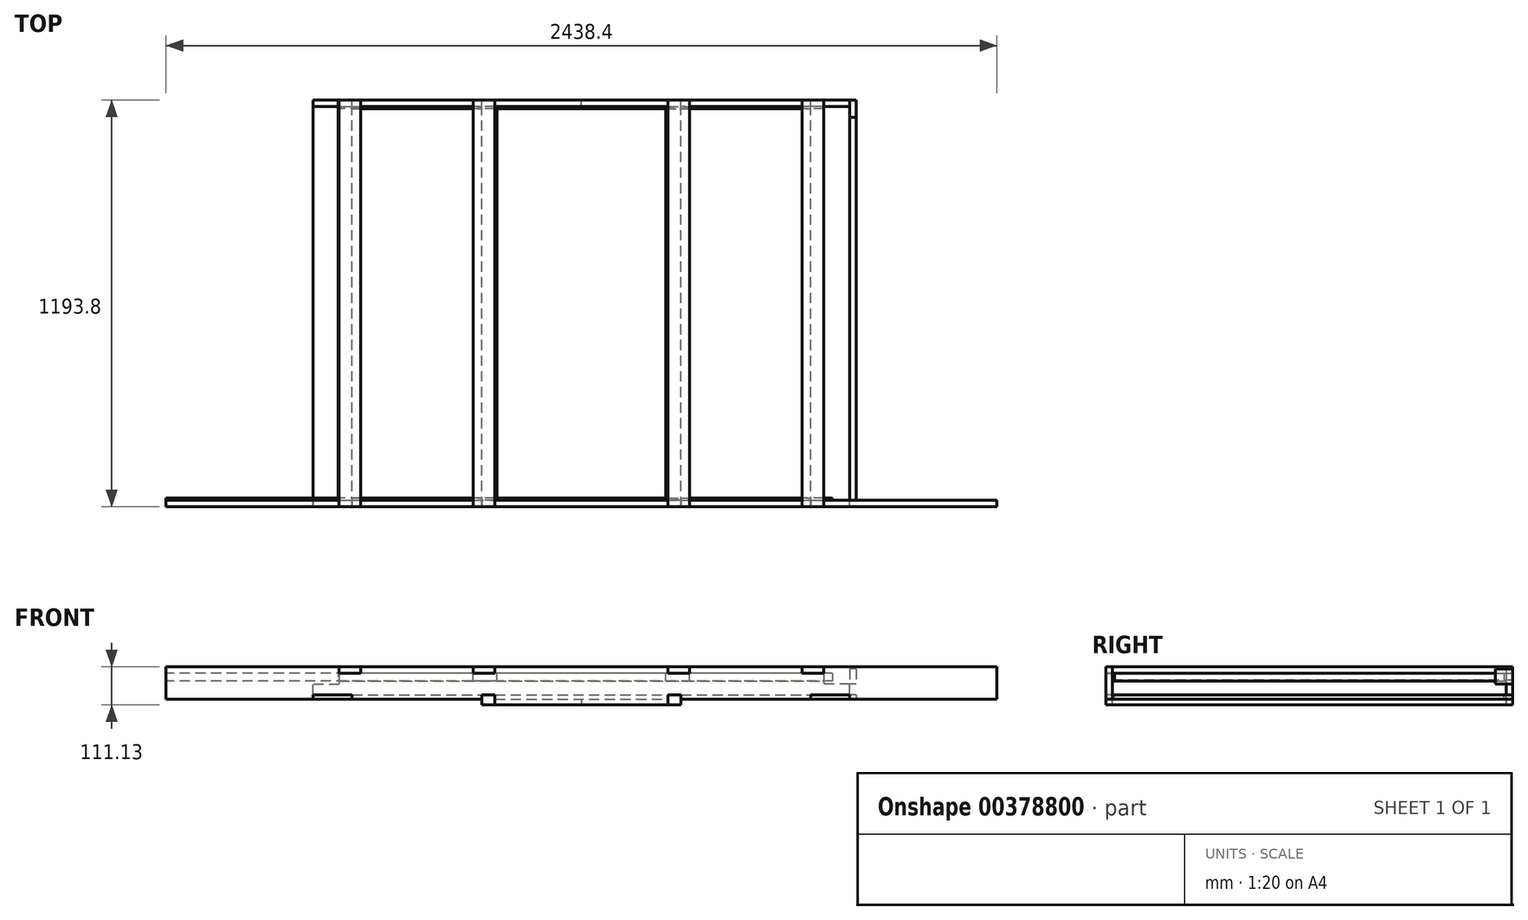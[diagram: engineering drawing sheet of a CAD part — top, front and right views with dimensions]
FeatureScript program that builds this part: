
annotation { "Feature Type Name" : "Feature", "Feature Type Description" : "" }
export const myFeature = defineFeature(function(context is Context, id is Id, definition is map)
    precondition{}
    {
        {
            var Q0;
            Q0=qCreatedBy(makeId("Front.planeOp"),FACE);
            var sketch = newSketch(context, id + "F0", { "sketchPlane" : qUnion([Q0])});
            skLineSegment(sketch, "E0.bottom", {"start": v(0, 0) * mm, "end": v(787.4, 0) * mm});
            skLineSegment(sketch, "E0.top", {"start": v(0, 95.25) * mm, "end": v(787.4, 95.25) * mm});
            skLineSegment(sketch, "E0.left", {"start": v(0, 0) * mm, "end": v(0, 95.25) * mm});
            skLineSegment(sketch, "E0.right", {"start": v(787.4, 0) * mm, "end": v(787.4, 95.25) * mm});
            skLineSegment(sketch, "E1.bottom", {"start": v(0, 95.25) * mm, "end": v(76.2, 95.25) * mm});
            skLineSegment(sketch, "E1.top", {"start": v(0, 44.45) * mm, "end": v(76.2, 44.45) * mm});
            skLineSegment(sketch, "E1.left", {"start": v(0, 95.25) * mm, "end": v(0, 44.45) * mm});
            skLineSegment(sketch, "E1.right", {"start": v(76.2, 95.25) * mm, "end": v(76.2, 44.45) * mm});
            skLineSegment(sketch, "E2.bottom", {"start": v(76.2, 95.25) * mm, "end": v(139.7, 95.25) * mm});
            skLineSegment(sketch, "E2.top", {"start": v(76.2, 76.2) * mm, "end": v(139.7, 76.2) * mm});
            skLineSegment(sketch, "E2.left", {"start": v(76.2, 95.25) * mm, "end": v(76.2, 76.2) * mm});
            skLineSegment(sketch, "E2.right", {"start": v(139.7, 95.25) * mm, "end": v(139.7, 76.2) * mm});
            skLineSegment(sketch, "E3.bottom", {"start": v(0, 0) * mm, "end": v(114.3, 0) * mm});
            skLineSegment(sketch, "E3.top", {"start": v(0, 12.7) * mm, "end": v(114.3, 12.7) * mm});
            skLineSegment(sketch, "E3.left", {"start": v(0, 0) * mm, "end": v(0, 12.7) * mm});
            skLineSegment(sketch, "E3.right", {"start": v(114.3, 0) * mm, "end": v(114.3, 12.7) * mm});
            skLineSegment(sketch, "E4.MirrorCS", {"start": v(1574.8, 0) * mm, "end": v(1574.8, 12.7) * mm});
            skLineSegment(sketch, "E5.MirrorCS", {"start": v(1498.6, 95.25) * mm, "end": v(1498.6, 76.2) * mm});
            skLineSegment(sketch, "E6.MirrorCS", {"start": v(1574.8, 0) * mm, "end": v(1574.8, 95.25) * mm});
            skLineSegment(sketch, "E7.MirrorCS", {"start": v(1498.6, 95.25) * mm, "end": v(1498.6, 44.45) * mm});
            skLineSegment(sketch, "E8.MirrorCS", {"start": v(1460.5, 0) * mm, "end": v(1460.5, 12.7) * mm});
            skLineSegment(sketch, "E9.MirrorCS", {"start": v(1435.1, 95.25) * mm, "end": v(1435.1, 76.2) * mm});
            skLineSegment(sketch, "E10.MirrorCS", {"start": v(1574.8, 44.45) * mm, "end": v(1498.6, 44.45) * mm});
            skLineSegment(sketch, "E11.MirrorCS", {"start": v(1574.8, 95.25) * mm, "end": v(1574.8, 44.45) * mm});
            skLineSegment(sketch, "E12.MirrorCS", {"start": v(1574.8, 95.25) * mm, "end": v(787.4, 95.25) * mm});
            skLineSegment(sketch, "E13.MirrorCS", {"start": v(1574.8, 0) * mm, "end": v(787.4, 0) * mm});
            skLineSegment(sketch, "E14.MirrorCS", {"start": v(1498.6, 76.2) * mm, "end": v(1435.1, 76.2) * mm});
            skLineSegment(sketch, "E15.MirrorCS", {"start": v(1574.8, 95.25) * mm, "end": v(1498.6, 95.25) * mm});
            skLineSegment(sketch, "E16.MirrorCS", {"start": v(1574.8, 0) * mm, "end": v(1460.5, 0) * mm});
            skLineSegment(sketch, "E17.MirrorCS", {"start": v(1498.6, 95.25) * mm, "end": v(1435.1, 95.25) * mm});
            skLineSegment(sketch, "E18.MirrorCS", {"start": v(1574.8, 12.7) * mm, "end": v(1460.5, 12.7) * mm});
            skLineSegment(sketch, "E19.bottom", {"start": v(533.4, 95.25) * mm, "end": v(469.9, 95.25) * mm});
            skLineSegment(sketch, "E19.top", {"start": v(533.4, 76.2) * mm, "end": v(469.9, 76.2) * mm});
            skLineSegment(sketch, "E19.left", {"start": v(533.4, 95.25) * mm, "end": v(533.4, 76.2) * mm});
            skLineSegment(sketch, "E19.right", {"start": v(469.9, 95.25) * mm, "end": v(469.9, 76.2) * mm});
            skLineSegment(sketch, "E20.MirrorCS", {"start": v(1041.4, 95.25) * mm, "end": v(1041.4, 76.2) * mm});
            skLineSegment(sketch, "E21.MirrorCS", {"start": v(1104.9, 95.25) * mm, "end": v(1104.9, 76.2) * mm});
            skLineSegment(sketch, "E22.MirrorCS", {"start": v(1041.4, 95.25) * mm, "end": v(1104.9, 95.25) * mm});
            skLineSegment(sketch, "E23.MirrorCS", {"start": v(1041.4, 76.2) * mm, "end": v(1104.9, 76.2) * mm});
            skLineSegment(sketch, "E24.bottom", {"start": v(533.4, 0) * mm, "end": v(495.3, 0) * mm});
            skLineSegment(sketch, "E24.top", {"start": v(533.4, 12.7) * mm, "end": v(495.3, 12.7) * mm});
            skLineSegment(sketch, "E24.left", {"start": v(533.4, 0) * mm, "end": v(533.4, 12.7) * mm});
            skLineSegment(sketch, "E24.right", {"start": v(495.3, 0) * mm, "end": v(495.3, 12.7) * mm});
            skLineSegment(sketch, "E25.bottom", {"start": v(787.4, 0) * mm, "end": v(533.4, 0) * mm});
            skLineSegment(sketch, "E25.top", {"start": v(787.4, -15.87) * mm, "end": v(533.4, -15.87) * mm});
            skLineSegment(sketch, "E25.left", {"start": v(787.4, 0) * mm, "end": v(787.4, -15.87) * mm});
            skLineSegment(sketch, "E25.right", {"start": v(533.4, 0) * mm, "end": v(533.4, -15.87) * mm});
            skLineSegment(sketch, "E26.MirrorCS", {"start": v(1079.5, 0) * mm, "end": v(1079.5, 12.7) * mm});
            skLineSegment(sketch, "E27.MirrorCS", {"start": v(1041.4, 0) * mm, "end": v(1041.4, 12.7) * mm});
            skLineSegment(sketch, "E28.MirrorCS", {"start": v(1041.4, 0) * mm, "end": v(1041.4, -15.87) * mm});
            skLineSegment(sketch, "E29.MirrorCS", {"start": v(1041.4, 0) * mm, "end": v(1079.5, 0) * mm});
            skLineSegment(sketch, "E30.MirrorCS", {"start": v(787.4, -15.87) * mm, "end": v(1041.4, -15.87) * mm});
            skLineSegment(sketch, "E31.MirrorCS", {"start": v(787.4, 0) * mm, "end": v(1041.4, 0) * mm});
            skLineSegment(sketch, "E32.MirrorCS", {"start": v(1041.4, 12.7) * mm, "end": v(1079.5, 12.7) * mm});
            skSolve(sketch);
        }
        {
            var Q0;
            Q0=makeQuery(id+"F0.imprint","IMPRINT",FACE,{"disambiguationData":[TD([[makeQuery(id+"F0.imprint","IMPRINT",EDGE,{"derivedFrom":sQuery(id+"F0.wireOp",EDGE,"E0.bottom")}),1.0]])]});
            var Q1;
            {var subQ1=sQuery(id+"F0.wireOp",EDGE,"E0.right");Q1=makeQuery(id+"F0.imprint","IMPRINT",FACE,{"disambiguationData":[TD([[makeQuery(id+"F0.imprint","IMPRINT",EDGE,{"derivedFrom":subQ1}),-1.0]])]});}
            var Q2;
            Q2=makeQuery(id+"F0.imprint","IMPRINT",FACE,{"disambiguationData":[TD([[makeQuery(id+"F0.imprint","IMPRINT",EDGE,{"derivedFrom":sQuery(id+"F0.wireOp",EDGE,"E25.bottom")}),1.0]])]});
            var Q3;
            Q3=makeQuery(id+"F0.imprint","IMPRINT",FACE,{"disambiguationData":[TD([[makeQuery(id+"F0.imprint","IMPRINT",EDGE,{"derivedFrom":sQuery(id+"F0.wireOp",EDGE,"E25.left")}),1.0]])]});
            extrude(context, id + "F1", {"entities" : qUnion([Q0, Q1, Q2, Q3]), "depth" : 19.05 * mm});
        }
        {
            var Q0;
            Q0=makeQuery(id+"F1.opExtrude","CAP_FACE",FACE,{"disambiguationData":[OSD([sQuery(id+"F0.wireOp",EDGE,"E0.bottom"),sQuery(id+"F0.wireOp",EDGE,"E0.top"),sQuery(id+"F0.wireOp",EDGE,"E0.left"),sQuery(id+"F0.wireOp",EDGE,"E1.top"),sQuery(id+"F0.wireOp",EDGE,"E1.right"),sQuery(id+"F0.wireOp",EDGE,"E2.top"),sQuery(id+"F0.wireOp",EDGE,"E2.right"),sQuery(id+"F0.wireOp",EDGE,"E3.top"),sQuery(id+"F0.wireOp",EDGE,"E3.right"),sQuery(id+"F0.wireOp",EDGE,"E6.MirrorCS"),sQuery(id+"F0.wireOp",EDGE,"E7.MirrorCS"),sQuery(id+"F0.wireOp",EDGE,"E8.MirrorCS"),sQuery(id+"F0.wireOp",EDGE,"E9.MirrorCS"),sQuery(id+"F0.wireOp",EDGE,"E10.MirrorCS"),sQuery(id+"F0.wireOp",EDGE,"E12.MirrorCS"),sQuery(id+"F0.wireOp",EDGE,"E13.MirrorCS"),sQuery(id+"F0.wireOp",EDGE,"E14.MirrorCS"),sQuery(id+"F0.wireOp",EDGE,"E18.MirrorCS"),sQuery(id+"F0.wireOp",EDGE,"E19.top"),sQuery(id+"F0.wireOp",EDGE,"E19.left"),sQuery(id+"F0.wireOp",EDGE,"E19.right"),sQuery(id+"F0.wireOp",EDGE,"E20.MirrorCS"),sQuery(id+"F0.wireOp",EDGE,"E21.MirrorCS"),sQuery(id+"F0.wireOp",EDGE,"E23.MirrorCS")])],"isStart":false});
            var sketch = newSketch(context, id + "F2", { "sketchPlane" : qUnion([Q0])});
            skLineSegment(sketch, "E33.bottom", {"start": v(114.3, 12.7) * mm, "end": v(1460.5, 12.7) * mm});
            skLineSegment(sketch, "E33.top", {"start": v(114.3, 0) * mm, "end": v(1460.5, 0) * mm});
            skLineSegment(sketch, "E33.left", {"start": v(114.3, 12.7) * mm, "end": v(114.3, 0) * mm});
            skLineSegment(sketch, "E33.right", {"start": v(1460.5, 12.7) * mm, "end": v(1460.5, 0) * mm});
            skSolve(sketch);
        }
        {
            var Q0;
            {var subQ0=sQuery(id+"F2.wireOp",EDGE,"E33.left");Q0=makeQuery(id+"F2.imprint","IMPRINT",FACE,{"disambiguationData":[TD([[makeQuery(id+"F2.imprint","IMPRINT",EDGE,{"derivedFrom":subQ0}),-1.0]])]});}
            var Q1;
            {var subQ0=sQuery(id+"F2.wireOp",EDGE,"E33.right");Q1=makeQuery(id+"F2.imprint","IMPRINT",FACE,{"disambiguationData":[TD([[makeQuery(id+"F2.imprint","IMPRINT",EDGE,{"derivedFrom":subQ0}),1.0]])]});}
            var Q2;
            {var subQ0=sQuery(id+"F2.wireOp",EDGE,"E33.bottom");var subQ1=makeQuery(id+"F1.opExtrude","CAP_EDGE",EDGE,{"disambiguationData":[OSD([sQuery(id+"F0.wireOp",EDGE,"E24.left"),sQuery(id+"F0.wireOp",EDGE,"E25.right")])],"isStart":false});var subQ2=makeQuery(id+"F2.imprint","INTERSECT",VERTEX,{"derivedFrom":[subQ1,subQ0]});var subQ3=makeQuery(id+"F1.opExtrude","CAP_EDGE",EDGE,{"disambiguationData":[OSD([sQuery(id+"F0.wireOp",EDGE,"E27.MirrorCS"),sQuery(id+"F0.wireOp",EDGE,"E28.MirrorCS")])],"isStart":false});var subQ4=makeQuery(id+"F2.imprint","INTERSECT",VERTEX,{"derivedFrom":[subQ3,subQ0]});Q2=makeQuery(id+"F2.imprint","IMPRINT",FACE,{"disambiguationData":[TD([[makeQuery(id+"F2.imprint","IMPRINT",EDGE,{"disambiguationData":[TD([[subQ2,-1.0],[subQ4,1.0]])],"derivedFrom":subQ0}),-1.0]])]});}
            extrude(context, id + "F3", {"entities" : qUnion([Q0, Q1, Q2]), "depth" : 6.35 * mm});
        }
        {
            var Q0;
            Q0=makeQuery(id+"F1.opExtrude","CAP_FACE",FACE,{"disambiguationData":[OSD([sQuery(id+"F0.wireOp",EDGE,"E0.bottom"),sQuery(id+"F0.wireOp",EDGE,"E0.top"),sQuery(id+"F0.wireOp",EDGE,"E0.left"),sQuery(id+"F0.wireOp",EDGE,"E1.top"),sQuery(id+"F0.wireOp",EDGE,"E1.right"),sQuery(id+"F0.wireOp",EDGE,"E2.top"),sQuery(id+"F0.wireOp",EDGE,"E2.right"),sQuery(id+"F0.wireOp",EDGE,"E3.top"),sQuery(id+"F0.wireOp",EDGE,"E3.right"),sQuery(id+"F0.wireOp",EDGE,"E6.MirrorCS"),sQuery(id+"F0.wireOp",EDGE,"E7.MirrorCS"),sQuery(id+"F0.wireOp",EDGE,"E8.MirrorCS"),sQuery(id+"F0.wireOp",EDGE,"E9.MirrorCS"),sQuery(id+"F0.wireOp",EDGE,"E10.MirrorCS"),sQuery(id+"F0.wireOp",EDGE,"E12.MirrorCS"),sQuery(id+"F0.wireOp",EDGE,"E13.MirrorCS"),sQuery(id+"F0.wireOp",EDGE,"E14.MirrorCS"),sQuery(id+"F0.wireOp",EDGE,"E18.MirrorCS"),sQuery(id+"F0.wireOp",EDGE,"E19.top"),sQuery(id+"F0.wireOp",EDGE,"E19.left"),sQuery(id+"F0.wireOp",EDGE,"E19.right"),sQuery(id+"F0.wireOp",EDGE,"E20.MirrorCS"),sQuery(id+"F0.wireOp",EDGE,"E21.MirrorCS"),sQuery(id+"F0.wireOp",EDGE,"E23.MirrorCS")])],"isStart":false});
            var sketch = newSketch(context, id + "F4", { "sketchPlane" : qUnion([Q0])});
            skLineSegment(sketch, "E34.bottom", {"start": v(76.2, 53.97) * mm, "end": v(1498.6, 53.97) * mm});
            skLineSegment(sketch, "E34.top", {"start": v(76.2, 76.2) * mm, "end": v(1498.6, 76.2) * mm});
            skLineSegment(sketch, "E34.left", {"start": v(76.2, 53.97) * mm, "end": v(76.2, 76.2) * mm});
            skLineSegment(sketch, "E34.right", {"start": v(1498.6, 53.97) * mm, "end": v(1498.6, 76.2) * mm});
            skSolve(sketch);
        }
        {
            var Q0;
            Q0=makeQuery(id+"F4.imprint","IMPRINT",FACE,{"disambiguationData":[TD([[makeQuery(id+"F4.imprint","IMPRINT",EDGE,{"derivedFrom":sQuery(id+"F4.wireOp",EDGE,"E34.bottom")}),1.0]])]});
            extrude(context, id + "F5", {"entities" : qUnion([Q0]), "depth" : 6.35 * mm});
        }
        {
            var Q0;
            Q0=qCreatedBy(makeId("Front.planeOp"),FACE);
            var sketch = newSketch(context, id + "F6", { "sketchPlane" : qUnion([Q0])});
            skLineSegment(sketch, "E35.bottom", {"start": v(139.7, 76.2) * mm, "end": v(76.2, 76.2) * mm});
            skLineSegment(sketch, "E35.top", {"start": v(139.7, 95.25) * mm, "end": v(76.2, 95.25) * mm});
            skLineSegment(sketch, "E35.left", {"start": v(139.7, 76.2) * mm, "end": v(139.7, 95.25) * mm});
            skLineSegment(sketch, "E35.right", {"start": v(76.2, 76.2) * mm, "end": v(76.2, 95.25) * mm});
            skLineSegment(sketch, "E36.bottom", {"start": v(469.9, 95.25) * mm, "end": v(533.4, 95.25) * mm});
            skLineSegment(sketch, "E36.top", {"start": v(469.9, 76.2) * mm, "end": v(533.4, 76.2) * mm});
            skLineSegment(sketch, "E36.left", {"start": v(469.9, 95.25) * mm, "end": v(469.9, 76.2) * mm});
            skLineSegment(sketch, "E36.right", {"start": v(533.4, 95.25) * mm, "end": v(533.4, 76.2) * mm});
            skLineSegment(sketch, "E37.bottom", {"start": v(1041.4, 76.2) * mm, "end": v(1104.9, 76.2) * mm});
            skLineSegment(sketch, "E37.top", {"start": v(1041.4, 95.25) * mm, "end": v(1104.9, 95.25) * mm});
            skLineSegment(sketch, "E37.left", {"start": v(1041.4, 76.2) * mm, "end": v(1041.4, 95.25) * mm});
            skLineSegment(sketch, "E37.right", {"start": v(1104.9, 76.2) * mm, "end": v(1104.9, 95.25) * mm});
            skLineSegment(sketch, "E38.bottom", {"start": v(1435.1, 76.2) * mm, "end": v(1498.6, 76.2) * mm});
            skLineSegment(sketch, "E38.top", {"start": v(1435.1, 95.25) * mm, "end": v(1498.6, 95.25) * mm});
            skLineSegment(sketch, "E38.left", {"start": v(1435.1, 76.2) * mm, "end": v(1435.1, 95.25) * mm});
            skLineSegment(sketch, "E38.right", {"start": v(1498.6, 76.2) * mm, "end": v(1498.6, 95.25) * mm});
            skLineSegment(sketch, "E39.bottom", {"start": v(1460.5, 0) * mm, "end": v(1574.8, 0) * mm});
            skLineSegment(sketch, "E39.top", {"start": v(1460.5, 12.7) * mm, "end": v(1574.8, 12.7) * mm});
            skLineSegment(sketch, "E39.left", {"start": v(1460.5, 0) * mm, "end": v(1460.5, 12.7) * mm});
            skLineSegment(sketch, "E39.right", {"start": v(1574.8, 0) * mm, "end": v(1574.8, 12.7) * mm});
            skLineSegment(sketch, "E40.bottom", {"start": v(114.3, 0) * mm, "end": v(0, 0) * mm});
            skLineSegment(sketch, "E40.top", {"start": v(114.3, 12.7) * mm, "end": v(0, 12.7) * mm});
            skLineSegment(sketch, "E40.left", {"start": v(114.3, 0) * mm, "end": v(114.3, 12.7) * mm});
            skLineSegment(sketch, "E40.right", {"start": v(0, 0) * mm, "end": v(0, 12.7) * mm});
            skLineSegment(sketch, "E41.bottom", {"start": v(533.4, -15.87) * mm, "end": v(495.3, -15.87) * mm});
            skLineSegment(sketch, "E41.top", {"start": v(533.4, 12.7) * mm, "end": v(495.3, 12.7) * mm});
            skLineSegment(sketch, "E41.left", {"start": v(533.4, -15.87) * mm, "end": v(533.4, 12.7) * mm});
            skLineSegment(sketch, "E41.right", {"start": v(495.3, -15.87) * mm, "end": v(495.3, 12.7) * mm});
            skLineSegment(sketch, "E42.bottom", {"start": v(1079.5, -15.87) * mm, "end": v(1041.4, -15.87) * mm});
            skLineSegment(sketch, "E42.top", {"start": v(1079.5, 12.7) * mm, "end": v(1041.4, 12.7) * mm});
            skLineSegment(sketch, "E42.left", {"start": v(1079.5, -15.87) * mm, "end": v(1079.5, 12.7) * mm});
            skLineSegment(sketch, "E42.right", {"start": v(1041.4, -15.87) * mm, "end": v(1041.4, 12.7) * mm});
            skSolve(sketch);
        }
        {
            var Q0;
            Q0=makeQuery(id+"F6.imprint","IMPRINT",FACE,{"disambiguationData":[TD([[makeQuery(id+"F6.imprint","IMPRINT",EDGE,{"derivedFrom":sQuery(id+"F6.wireOp",EDGE,"E35.bottom")}),-1.0]])]});
            var Q1;
            Q1=makeQuery(id+"F6.imprint","IMPRINT",FACE,{"disambiguationData":[TD([[makeQuery(id+"F6.imprint","IMPRINT",EDGE,{"derivedFrom":sQuery(id+"F6.wireOp",EDGE,"E36.bottom")}),-1.0]])]});
            var Q2;
            Q2=makeQuery(id+"F6.imprint","IMPRINT",FACE,{"disambiguationData":[TD([[makeQuery(id+"F6.imprint","IMPRINT",EDGE,{"derivedFrom":sQuery(id+"F6.wireOp",EDGE,"E38.bottom")}),1.0]])]});
            var Q3;
            Q3=makeQuery(id+"F6.imprint","IMPRINT",FACE,{"disambiguationData":[TD([[makeQuery(id+"F6.imprint","IMPRINT",EDGE,{"derivedFrom":sQuery(id+"F6.wireOp",EDGE,"E37.bottom")}),1.0]])]});
            var Q4;
            Q4=makeQuery(id+"F6.imprint","IMPRINT",FACE,{"disambiguationData":[TD([[makeQuery(id+"F6.imprint","IMPRINT",EDGE,{"derivedFrom":sQuery(id+"F6.wireOp",EDGE,"E39.bottom")}),1.0]])]});
            var Q5;
            Q5=makeQuery(id+"F6.imprint","IMPRINT",FACE,{"disambiguationData":[TD([[makeQuery(id+"F6.imprint","IMPRINT",EDGE,{"derivedFrom":sQuery(id+"F6.wireOp",EDGE,"E40.bottom")}),-1.0]])]});
            var Q6;
            Q6=makeQuery(id+"F6.imprint","IMPRINT",FACE,{"disambiguationData":[TD([[makeQuery(id+"F6.imprint","IMPRINT",EDGE,{"derivedFrom":sQuery(id+"F6.wireOp",EDGE,"E41.bottom")}),-1.0]])]});
            var Q7;
            Q7=makeQuery(id+"F6.imprint","IMPRINT",FACE,{"disambiguationData":[TD([[makeQuery(id+"F6.imprint","IMPRINT",EDGE,{"derivedFrom":sQuery(id+"F6.wireOp",EDGE,"E42.bottom")}),-1.0]])]});
            extrude(context, id + "F7", {"entities" : qUnion([Q0, Q1, Q2, Q3, Q4, Q5, Q6, Q7]), "depth" : 1193.8 * mm});
        }
        {
            var Q0;
            Q0=makeQuery(id+"F7.opExtrude","CAP_FACE",FACE,{"disambiguationData":[OSD([sQuery(id+"F6.wireOp",EDGE,"E38.bottom"),sQuery(id+"F6.wireOp",EDGE,"E38.top"),sQuery(id+"F6.wireOp",EDGE,"E38.left"),sQuery(id+"F6.wireOp",EDGE,"E38.right")])],"isStart":false});
            var sketch = newSketch(context, id + "F8", { "sketchPlane" : qUnion([Q0])});
            skLineSegment(sketch, "E43.bottom", {"start": v(292.1, 95.25) * mm, "end": v(-431.8, 95.25) * mm});
            skLineSegment(sketch, "E43.top", {"start": v(317.5, 0) * mm, "end": v(-431.8, 0) * mm});
            skLineSegment(sketch, "E43.right", {"start": v(-431.8, 95.25) * mm, "end": v(-431.8, 0) * mm});
            skLineSegment(sketch, "E44.bottom", {"start": v(76.2, 95.25) * mm, "end": v(139.7, 95.25) * mm});
            skLineSegment(sketch, "E44.top", {"start": v(76.2, 76.2) * mm, "end": v(139.7, 76.2) * mm});
            skLineSegment(sketch, "E44.left", {"start": v(76.2, 95.25) * mm, "end": v(76.2, 76.2) * mm});
            skLineSegment(sketch, "E44.right", {"start": v(139.7, 95.25) * mm, "end": v(139.7, 76.2) * mm});
            skLineSegment(sketch, "E45.bottom", {"start": v(469.9, 95.25) * mm, "end": v(533.4, 95.25) * mm});
            skLineSegment(sketch, "E45.top", {"start": v(469.9, 76.2) * mm, "end": v(533.4, 76.2) * mm});
            skLineSegment(sketch, "E45.left", {"start": v(469.9, 95.25) * mm, "end": v(469.9, 76.2) * mm});
            skLineSegment(sketch, "E45.right", {"start": v(533.4, 95.25) * mm, "end": v(533.4, 76.2) * mm});
            skLineSegment(sketch, "E46.MirrorCS", {"start": v(533.4, 76.2) * mm, "end": v(469.9, 76.2) * mm});
            skLineSegment(sketch, "E47.MirrorCS", {"start": v(139.7, 76.2) * mm, "end": v(76.2, 76.2) * mm});
            skLineSegment(sketch, "E48.MirrorCS", {"start": v(139.7, 95.25) * mm, "end": v(76.2, 95.25) * mm});
            skLineSegment(sketch, "E49.MirrorCS", {"start": v(533.4, 95.25) * mm, "end": v(469.9, 95.25) * mm});
            skLineSegment(sketch, "E50.bottom", {"start": v(1460.5, 0) * mm, "end": v(1574.8, 0) * mm});
            skLineSegment(sketch, "E50.top", {"start": v(1460.5, 12.7) * mm, "end": v(1574.8, 12.7) * mm});
            skLineSegment(sketch, "E50.left", {"start": v(1460.5, 0) * mm, "end": v(1460.5, 12.7) * mm});
            skLineSegment(sketch, "E50.right", {"start": v(1574.8, 0) * mm, "end": v(1574.8, 12.7) * mm});
            skLineSegment(sketch, "E51.bottom", {"start": v(0, 12.7) * mm, "end": v(114.3, 12.7) * mm});
            skLineSegment(sketch, "E51.top", {"start": v(0, 0) * mm, "end": v(114.3, 0) * mm});
            skLineSegment(sketch, "E51.left", {"start": v(0, 12.7) * mm, "end": v(0, 0) * mm});
            skLineSegment(sketch, "E51.right", {"start": v(114.3, 12.7) * mm, "end": v(114.3, 0) * mm});
            skLineSegment(sketch, "E52", {"start": v(787.4, 95.25) * mm, "end": v(787.4, 0) * mm});
            skLineSegment(sketch, "E53", {"start": v(787.4, 95.25) * mm, "end": v(292.1, 95.25) * mm});
            skLineSegment(sketch, "E54", {"start": v(787.4, 0) * mm, "end": v(317.5, 0) * mm});
            skLineSegment(sketch, "E55.MirrorCS", {"start": v(1498.6, 95.25) * mm, "end": v(1498.6, 76.2) * mm});
            skLineSegment(sketch, "E56.MirrorCS", {"start": v(1104.9, 95.25) * mm, "end": v(1104.9, 76.2) * mm});
            skLineSegment(sketch, "E57.MirrorCS", {"start": v(1041.4, 95.25) * mm, "end": v(1041.4, 76.2) * mm});
            skLineSegment(sketch, "E58.MirrorCS", {"start": v(1104.9, 95.25) * mm, "end": v(1041.4, 95.25) * mm});
            skLineSegment(sketch, "E59.MirrorCS", {"start": v(1435.1, 95.25) * mm, "end": v(1435.1, 76.2) * mm});
            skLineSegment(sketch, "E60.MirrorCS", {"start": v(1041.4, 76.2) * mm, "end": v(1104.9, 76.2) * mm});
            skLineSegment(sketch, "E61.MirrorCS", {"start": v(1435.1, 76.2) * mm, "end": v(1498.6, 76.2) * mm});
            skLineSegment(sketch, "E62.MirrorCS", {"start": v(1498.6, 76.2) * mm, "end": v(1435.1, 76.2) * mm});
            skLineSegment(sketch, "E63.MirrorCS", {"start": v(1574.8, 12.7) * mm, "end": v(1574.8, 0) * mm});
            skLineSegment(sketch, "E64.MirrorCS", {"start": v(1498.6, 95.25) * mm, "end": v(1435.1, 95.25) * mm});
            skLineSegment(sketch, "E65.MirrorCS", {"start": v(1435.1, 95.25) * mm, "end": v(1498.6, 95.25) * mm});
            skLineSegment(sketch, "E66.MirrorCS", {"start": v(1460.5, 12.7) * mm, "end": v(1460.5, 0) * mm});
            skLineSegment(sketch, "E67.MirrorCS", {"start": v(1041.4, 95.25) * mm, "end": v(1104.9, 95.25) * mm});
            skLineSegment(sketch, "E68.MirrorCS", {"start": v(1104.9, 76.2) * mm, "end": v(1041.4, 76.2) * mm});
            skLineSegment(sketch, "E69.MirrorCS", {"start": v(1282.7, 95.25) * mm, "end": v(2006.6, 95.25) * mm});
            skLineSegment(sketch, "E70.MirrorCS", {"start": v(1257.3, 0) * mm, "end": v(2006.6, 0) * mm});
            skLineSegment(sketch, "E71.MirrorCS", {"start": v(1574.8, 12.7) * mm, "end": v(1460.5, 12.7) * mm});
            skLineSegment(sketch, "E72.MirrorCS", {"start": v(1574.8, 0) * mm, "end": v(1460.5, 0) * mm});
            skLineSegment(sketch, "E73.MirrorCS", {"start": v(787.4, 95.25) * mm, "end": v(1282.7, 95.25) * mm});
            skLineSegment(sketch, "E74.MirrorCS", {"start": v(2006.6, 95.25) * mm, "end": v(2006.6, 0) * mm});
            skLineSegment(sketch, "E75.MirrorCS", {"start": v(787.4, 0) * mm, "end": v(1257.3, 0) * mm});
            skLineSegment(sketch, "E76.bottom", {"start": v(1079.5, -15.87) * mm, "end": v(1041.4, -15.87) * mm});
            skLineSegment(sketch, "E76.top", {"start": v(1079.5, 12.7) * mm, "end": v(1041.4, 12.7) * mm});
            skLineSegment(sketch, "E76.left", {"start": v(1079.5, -15.87) * mm, "end": v(1079.5, 12.7) * mm});
            skLineSegment(sketch, "E76.right", {"start": v(1041.4, -15.87) * mm, "end": v(1041.4, 12.7) * mm});
            skLineSegment(sketch, "E77.bottom", {"start": v(533.4, -15.87) * mm, "end": v(495.3, -15.87) * mm});
            skLineSegment(sketch, "E77.top", {"start": v(533.4, 12.7) * mm, "end": v(495.3, 12.7) * mm});
            skLineSegment(sketch, "E77.left", {"start": v(533.4, -15.87) * mm, "end": v(533.4, 12.7) * mm});
            skLineSegment(sketch, "E77.right", {"start": v(495.3, -15.87) * mm, "end": v(495.3, 12.7) * mm});
            skLineSegment(sketch, "E78.bottom", {"start": v(1041.4, -15.87) * mm, "end": v(533.4, -15.87) * mm});
            skLineSegment(sketch, "E78.top", {"start": v(1041.4, 0) * mm, "end": v(533.4, 0) * mm});
            skLineSegment(sketch, "E78.left", {"start": v(1041.4, -15.87) * mm, "end": v(1041.4, 0) * mm});
            skLineSegment(sketch, "E78.right", {"start": v(533.4, -15.87) * mm, "end": v(533.4, 0) * mm});
            skSolve(sketch);
        }
        {
            var Q0;
            Q0=makeQuery(id+"F8.imprint","IMPRINT",FACE,{"disambiguationData":[TD([[makeQuery(id+"F8.imprint","IMPRINT",EDGE,{"derivedFrom":sQuery(id+"F8.wireOp",EDGE,"E43.top")}),-1.0]])]});
            var Q1;
            {var subQ7=sQuery(id+"F8.wireOp",EDGE,"E43.left");Q1=makeQuery(id+"F8.imprint","IMPRINT",FACE,{"disambiguationData":[TD([[makeQuery(id+"F8.imprint","IMPRINT",EDGE,{"derivedFrom":subQ7}),1.0]])]});}
            var Q2;
            {var subQ14=sQuery(id+"F8.wireOp",EDGE,"E52");Q2=makeQuery(id+"F8.imprint","IMPRINT",FACE,{"disambiguationData":[TD([[makeQuery(id+"F8.imprint","IMPRINT",EDGE,{"derivedFrom":subQ14}),1.0]])]});}
            var Q3;
            Q3=makeQuery(id+"F8.imprint","IMPRINT",FACE,{"disambiguationData":[TD([[makeQuery(id+"F8.imprint","IMPRINT",EDGE,{"derivedFrom":sQuery(id+"F8.wireOp",EDGE,"E78.bottom")}),-1.0]])]});
            extrude(context, id + "F9", {"entities" : qUnion([Q0, Q1, Q2, Q3]), "depth" : -19.05 * mm});
        }
        {
            var Q0;
            Q0=makeQuery(id+"F9.opExtrude","CAP_FACE",FACE,{"disambiguationData":[OSD([sQuery(id+"F8.wireOp",EDGE,"E43.bottom"),sQuery(id+"F8.wireOp",EDGE,"E43.top"),sQuery(id+"F8.wireOp",EDGE,"E43.right"),sQuery(id+"F8.wireOp",EDGE,"E44.top"),sQuery(id+"F8.wireOp",EDGE,"E44.left"),sQuery(id+"F8.wireOp",EDGE,"E44.right"),sQuery(id+"F8.wireOp",EDGE,"E45.top"),sQuery(id+"F8.wireOp",EDGE,"E45.left"),sQuery(id+"F8.wireOp",EDGE,"E45.right"),sQuery(id+"F8.wireOp",EDGE,"E45.right"),sQuery(id+"F8.wireOp",EDGE,"E44.right"),sQuery(id+"F8.wireOp",EDGE,"E44.left"),sQuery(id+"F8.wireOp",EDGE,"E45.left"),sQuery(id+"F8.wireOp",EDGE,"E46.MirrorCS"),sQuery(id+"F8.wireOp",EDGE,"4a7b3bc9-8c18-4842-b5df-dcdeadcb97185.MirrorCS"),sQuery(id+"F8.wireOp",EDGE,"4a7b3bc9-8c18-4842-b5df-dcdeadcb97186.MirrorCS"),sQuery(id+"F8.wireOp",EDGE,"4a7b3bc9-8c18-4842-b5df-dcdeadcb97187.MirrorCS"),sQuery(id+"F8.wireOp",EDGE,"E47.MirrorCS")])],"isStart":false});
            var sketch = newSketch(context, id + "F10", { "sketchPlane" : qUnion([Q0])});
            skLineSegment(sketch, "E79.bottom", {"start": v(-1524, 76.2) * mm, "end": v(431.8, 76.2) * mm});
            skLineSegment(sketch, "E79.top", {"start": v(-1524, 53.98) * mm, "end": v(431.8, 53.98) * mm});
            skLineSegment(sketch, "E79.left", {"start": v(-1524, 76.2) * mm, "end": v(-1524, 53.98) * mm});
            skLineSegment(sketch, "E79.right", {"start": v(431.8, 76.2) * mm, "end": v(431.8, 53.98) * mm});
            skSolve(sketch);
        }
        {
            var Q0;
            Q0 = qSketchRegion(id + "F10", true);
            extrude(context, id + "F11", {"entities" : qUnion([Q0]), "depth" : 6.35 * mm});
        }
        {
            var Q0;
            Q0=makeQuery(id+"F9.opExtrude","CAP_FACE",FACE,{"disambiguationData":[OSD([sQuery(id+"F8.wireOp",EDGE,"E43.bottom"),sQuery(id+"F8.wireOp",EDGE,"E43.top"),sQuery(id+"F8.wireOp",EDGE,"E43.right"),sQuery(id+"F8.wireOp",EDGE,"E45.right"),sQuery(id+"F8.wireOp",EDGE,"E44.right"),sQuery(id+"F8.wireOp",EDGE,"E44.left"),sQuery(id+"F8.wireOp",EDGE,"E45.left"),sQuery(id+"F8.wireOp",EDGE,"E46.MirrorCS"),sQuery(id+"F8.wireOp",EDGE,"E47.MirrorCS"),sQuery(id+"F8.wireOp",EDGE,"E51.bottom"),sQuery(id+"F8.wireOp",EDGE,"E51.left"),sQuery(id+"F8.wireOp",EDGE,"E51.right"),sQuery(id+"F8.wireOp",EDGE,"E53"),sQuery(id+"F8.wireOp",EDGE,"E54"),sQuery(id+"F8.wireOp",EDGE,"E57.MirrorCS"),sQuery(id+"F8.wireOp",EDGE,"E55.MirrorCS"),sQuery(id+"F8.wireOp",EDGE,"E62.MirrorCS"),sQuery(id+"F8.wireOp",EDGE,"E59.MirrorCS"),sQuery(id+"F8.wireOp",EDGE,"E63.MirrorCS"),sQuery(id+"F8.wireOp",EDGE,"E66.MirrorCS"),sQuery(id+"F8.wireOp",EDGE,"E56.MirrorCS"),sQuery(id+"F8.wireOp",EDGE,"E68.MirrorCS"),sQuery(id+"F8.wireOp",EDGE,"E69.MirrorCS"),sQuery(id+"F8.wireOp",EDGE,"E70.MirrorCS"),sQuery(id+"F8.wireOp",EDGE,"E71.MirrorCS"),sQuery(id+"F8.wireOp",EDGE,"E73.MirrorCS"),sQuery(id+"F8.wireOp",EDGE,"E74.MirrorCS"),sQuery(id+"F8.wireOp",EDGE,"E75.MirrorCS"),sQuery(id+"F8.wireOp",EDGE,"E76.top"),sQuery(id+"F8.wireOp",EDGE,"E76.left"),sQuery(id+"F8.wireOp",EDGE,"E76.right"),sQuery(id+"F8.wireOp",EDGE,"E77.top"),sQuery(id+"F8.wireOp",EDGE,"E77.left"),sQuery(id+"F8.wireOp",EDGE,"E77.right"),sQuery(id+"F8.wireOp",EDGE,"E78.bottom"),sQuery(id+"F8.wireOp",EDGE,"E78.left"),sQuery(id+"F8.wireOp",EDGE,"E78.right")])],"isStart":false});
            var sketch = newSketch(context, id + "F12", { "sketchPlane" : qUnion([Q0])});
            skLineSegment(sketch, "E80", {"start": v(-1079.5, 12.7) * mm, "end": v(-1460.5, 12.7) * mm});
            skLineSegment(sketch, "E81", {"start": v(-1460.5, 12.7) * mm, "end": v(-1460.5, 0) * mm});
            skLineSegment(sketch, "E82", {"start": v(-1460.5, 0) * mm, "end": v(-1079.5, 0) * mm});
            skLineSegment(sketch, "E83", {"start": v(-1079.5, 0) * mm, "end": v(-1079.5, 12.7) * mm});
            skLineSegment(sketch, "E84", {"start": v(-495.3, 12.7) * mm, "end": v(-495.3, 0) * mm});
            skLineSegment(sketch, "E85", {"start": v(-114.3, 0) * mm, "end": v(-114.3, 12.7) * mm});
            skLineSegment(sketch, "E86", {"start": v(-114.3, 12.7) * mm, "end": v(-495.3, 12.7) * mm});
            skLineSegment(sketch, "E87", {"start": v(-495.3, 0) * mm, "end": v(-114.3, 0) * mm});
            skLineSegment(sketch, "E88", {"start": v(-1041.4, 12.7) * mm, "end": v(-533.4, 12.7) * mm});
            skLineSegment(sketch, "E89", {"start": v(-533.4, 12.7) * mm, "end": v(-533.4, 0) * mm});
            skLineSegment(sketch, "E90", {"start": v(-533.4, 0) * mm, "end": v(-1041.4, 0) * mm});
            skLineSegment(sketch, "E91", {"start": v(-1041.4, 0) * mm, "end": v(-1041.4, 12.7) * mm});
            skSolve(sketch);
        }
        {
            var Q0;
            Q0=makeQuery(id+"F12.imprint","IMPRINT",FACE,{"disambiguationData":[TD([[makeQuery(id+"F12.imprint","IMPRINT",EDGE,{"derivedFrom":sQuery(id+"F12.wireOp",EDGE,"E80")}),1.0]])]});
            var Q1;
            Q1=makeQuery(id+"F12.imprint","IMPRINT",FACE,{"disambiguationData":[TD([[makeQuery(id+"F12.imprint","IMPRINT",EDGE,{"derivedFrom":sQuery(id+"F12.wireOp",EDGE,"E84")}),-1.0]])]});
            var Q2;
            Q2=makeQuery(id+"F12.imprint","IMPRINT",FACE,{"disambiguationData":[TD([[makeQuery(id+"F12.imprint","IMPRINT",EDGE,{"derivedFrom":sQuery(id+"F12.wireOp",EDGE,"E88")}),-1.0]])]});
            extrude(context, id + "F13", {"entities" : qUnion([Q0, Q1, Q2]), "depth" : 6.35 * mm});
        }
        {
            var Q0;
            Q0=makeQuery(id+"F7.opExtrude","SWEPT_FACE",FACE,{"disambiguationData":[OSD([sQuery(id+"F6.wireOp",EDGE,"E37.bottom")])]});
            var sketch = newSketch(context, id + "F14", { "sketchPlane" : qUnion([Q0])});
            skLineSegment(sketch, "E92.bottom", {"start": v(1035.05, 1168.4) * mm, "end": v(1104.9, 1168.4) * mm});
            skLineSegment(sketch, "E92.top", {"start": v(1035.05, 25.4) * mm, "end": v(1104.9, 25.4) * mm});
            skLineSegment(sketch, "E92.left", {"start": v(1035.05, 1168.4) * mm, "end": v(1035.05, 25.4) * mm});
            skLineSegment(sketch, "E92.right", {"start": v(1104.9, 1168.4) * mm, "end": v(1104.9, 25.4) * mm});
            skSolve(sketch);
        }
        {
            var Q0;
            Q0 = qSketchRegion(id + "F14", true);
            extrude(context, id + "F15", {"entities" : qUnion([Q0]), "depth" : 22.22 * mm});
        }
        {
            var Q0;
            Q0=makeQuery(id+"F7.opExtrude","SWEPT_FACE",FACE,{"disambiguationData":[OSD([sQuery(id+"F6.wireOp",EDGE,"E36.top")])]});
            var sketch = newSketch(context, id + "F16", { "sketchPlane" : qUnion([Q0])});
            skLineSegment(sketch, "E93.bottom", {"start": v(539.75, 1168.4) * mm, "end": v(469.9, 1168.4) * mm});
            skLineSegment(sketch, "E93.top", {"start": v(539.75, 25.4) * mm, "end": v(469.9, 25.4) * mm});
            skLineSegment(sketch, "E93.left", {"start": v(539.75, 1168.4) * mm, "end": v(539.75, 25.4) * mm});
            skLineSegment(sketch, "E93.right", {"start": v(469.9, 1168.4) * mm, "end": v(469.9, 25.4) * mm});
            skSolve(sketch);
        }
        {
            var Q0;
            Q0 = qSketchRegion(id + "F16", true);
            extrude(context, id + "F17", {"entities" : qUnion([Q0]), "depth" : 22.22 * mm});
        }
        {
            var Q0;
            Q0=makeQuery(id+"F7.opExtrude","SWEPT_FACE",FACE,{"disambiguationData":[OSD([sQuery(id+"F6.wireOp",EDGE,"E35.right")])]});
            var sketch = newSketch(context, id + "F18", { "sketchPlane" : qUnion([Q0])});
            skLineSegment(sketch, "E94.bottom", {"start": v(1174.75, 95.25) * mm, "end": v(0, 95.25) * mm});
            skLineSegment(sketch, "E94.top", {"start": v(1174.75, 57.15) * mm, "end": v(0, 57.15) * mm});
            skLineSegment(sketch, "E94.left", {"start": v(1174.75, 95.25) * mm, "end": v(1174.75, 57.15) * mm});
            skLineSegment(sketch, "E94.right", {"start": v(0, 95.25) * mm, "end": v(0, 57.15) * mm});
            skLineSegment(sketch, "E95.bottom", {"start": v(1174.75, 57.15) * mm, "end": v(1168.4, 57.15) * mm});
            skLineSegment(sketch, "E95.top", {"start": v(1174.75, 76.2) * mm, "end": v(1168.4, 76.2) * mm});
            skLineSegment(sketch, "E95.left", {"start": v(1174.75, 57.15) * mm, "end": v(1174.75, 76.2) * mm});
            skLineSegment(sketch, "E95.right", {"start": v(1168.4, 57.15) * mm, "end": v(1168.4, 76.2) * mm});
            skSolve(sketch);
        }
        {
            var Q0;
            {var subQ0=sQuery(id+"F18.wireOp",EDGE,"E94.top");Q0=makeQuery(id+"F18.imprint","IMPRINT",FACE,{"disambiguationData":[TD([[makeQuery(id+"F18.imprint","IMPRINT",EDGE,{"derivedFrom":subQ0}),-1.0]])]});}
            var Q1;
            {var subQ0=sQuery(id+"F18.wireOp",EDGE,"E94.bottom");Q1=makeQuery(id+"F18.imprint","IMPRINT",FACE,{"disambiguationData":[TD([[makeQuery(id+"F18.imprint","IMPRINT",EDGE,{"derivedFrom":subQ0}),1.0]])]});}
            extrude(context, id + "F19", {"entities" : qUnion([Q0, Q1]), "depth" : 3.17 * mm});
        }
        {
            var Q0;
            Q0=makeQuery(id+"F7.opExtrude","SWEPT_FACE",FACE,{"disambiguationData":[OSD([sQuery(id+"F6.wireOp",EDGE,"E39.right")])]});
            var sketch = newSketch(context, id + "F20", { "sketchPlane" : qUnion([Q0])});
            skLineSegment(sketch, "E96.bottom", {"start": v(-1174.75, 88.9) * mm, "end": v(0, 88.9) * mm});
            skLineSegment(sketch, "E96.top", {"start": v(-1174.75, 0) * mm, "end": v(0, 0) * mm});
            skLineSegment(sketch, "E96.left", {"start": v(-1174.75, 88.9) * mm, "end": v(-1174.75, 0) * mm});
            skLineSegment(sketch, "E96.right", {"start": v(0, 88.9) * mm, "end": v(0, 0) * mm});
            skLineSegment(sketch, "E97.bottom", {"start": v(-50.8, 88.9) * mm, "end": v(0, 88.9) * mm});
            skLineSegment(sketch, "E97.top", {"start": v(-50.8, 44.45) * mm, "end": v(0, 44.45) * mm});
            skLineSegment(sketch, "E97.left", {"start": v(-50.8, 88.9) * mm, "end": v(-50.8, 44.45) * mm});
            skLineSegment(sketch, "E97.right", {"start": v(0, 88.9) * mm, "end": v(0, 44.45) * mm});
            skLineSegment(sketch, "E98.bottom", {"start": v(-1174.75, 57.15) * mm, "end": v(-1162.05, 57.15) * mm});
            skLineSegment(sketch, "E98.top", {"start": v(-1174.75, 12.7) * mm, "end": v(-1162.05, 12.7) * mm});
            skLineSegment(sketch, "E98.left", {"start": v(-1174.75, 57.15) * mm, "end": v(-1174.75, 12.7) * mm});
            skLineSegment(sketch, "E98.right", {"start": v(-1162.05, 57.15) * mm, "end": v(-1162.05, 12.7) * mm});
            skSolve(sketch);
        }
        {
            var Q0;
            {var subQ0=sQuery(id+"F20.wireOp",EDGE,"E96.top");Q0=makeQuery(id+"F20.imprint","IMPRINT",FACE,{"disambiguationData":[TD([[makeQuery(id+"F20.imprint","IMPRINT",EDGE,{"derivedFrom":subQ0}),1.0]])]});}
            var Q1;
            {var subQ0=sQuery(id+"F20.wireOp",EDGE,"E96.bottom");Q1=makeQuery(id+"F20.imprint","IMPRINT",FACE,{"disambiguationData":[TD([[makeQuery(id+"F20.imprint","IMPRINT",EDGE,{"derivedFrom":subQ0}),-1.0]])]});}
            extrude(context, id + "F21", {"entities" : qUnion([Q0, Q1]), "depth" : 19.05 * mm});
        }
    });
